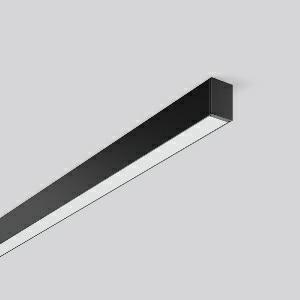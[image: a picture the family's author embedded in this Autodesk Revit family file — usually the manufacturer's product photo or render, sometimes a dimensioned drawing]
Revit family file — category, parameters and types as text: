
# Revit family: less_is_more_27_312199_003_1_76_6d48
name_source: partatom
category: Lighting Fixtures
units: mm (PartAtom-declared; Revit-internal decimal feet)

## family parameters
Cut with Voids When Loaded = No
Host = Face
Light Source = No
Part Type = Normal
Room Calculation Point = No
Round Connector Dimension = Use Diameter
Shared = No

## types (1)
- LESS IS MORE 27 (1 x LED Modul 840, 2200 lm, 4000)
    Apparent Load = 31 VA
    CIE Flux Codes = 65 89 98 100 100
    Color Rendering = 80
    Color Temperature = 4000
    Default Elevation = 1800 mm
    Description = Series: LESS IS MORE 27
Ceiling luminaire with slim design. Housing: extruded aluminium profile, powder-coated. End cap aluminium powder-coated. Diffuser made of non-yellowing plastic (PMMA) microprismatic. Suitable for Ceiling mounting, Wall (surface). External driver with connecting cable. 
Colour: deep black, matt (RAL 9005)
Length: 1212 mm
Width: 28 mm
Height: 38 mm
Lamp: LED
Socket: without socket
Colour temperature: 4000K
Colour rendering index (CRI): 82
System power: 31 W
Rated luminous flux: 2200 lm
Luminous efficiency: 71 lm/W
Control gear: Voltage converter, DALI dim.
Protection class: II
Type of protection: IP 20
    Height = 38 mm
    Lamp = 1 x LED Modul 840
    Lamp Light Flux = 2200 lm
    Lamp count = 1
    Length = 1212 mm
    Lifetime = 50000 h
    Luminous efficacy = 71 lm/W
    Manufacturer = RZB
    ModVariant = No
    Model = 312199.003.1.76
    Mounting Place = Ceiling, Wall
    Mounting Type = Surface mounted
    Number of Poles = 1
    OnlyDefault = Yes
    Power Factor = 1
    Product Name = LESS IS MORE 27
    Product group = Surface mounted LED linear luminaires
    ProductGroupID = 307
    Protection Class = Protection class II
    Protection Degree = IP 20
    RLX_Detail_Level = 1
    RLX_Emergency_Light_Flux = 0 lm
    RLX_Emergency_Type = 0
    RLX_Emergency_Type_DB = No
    RlxData = <blob elided: 29741 chars, md5=62a5920c>
    Socket = socket
    Standby Power = 0 W
    System Light Flux = 2200 lm
    System Power = 31 W
    Type Comments = Product without accessories
    Type Image = 312196.003.jpg
    URL = http://relux.com
    VarID = ---
    Voltage = 230 V
    Voltage Range = 220-240 V
    Weight = 0.00 kg
    Width = 28 mm

## geometry (parser evidence)
native form markers: Blend x4, Sweep x9
no freeform markers — native parametric forms only
